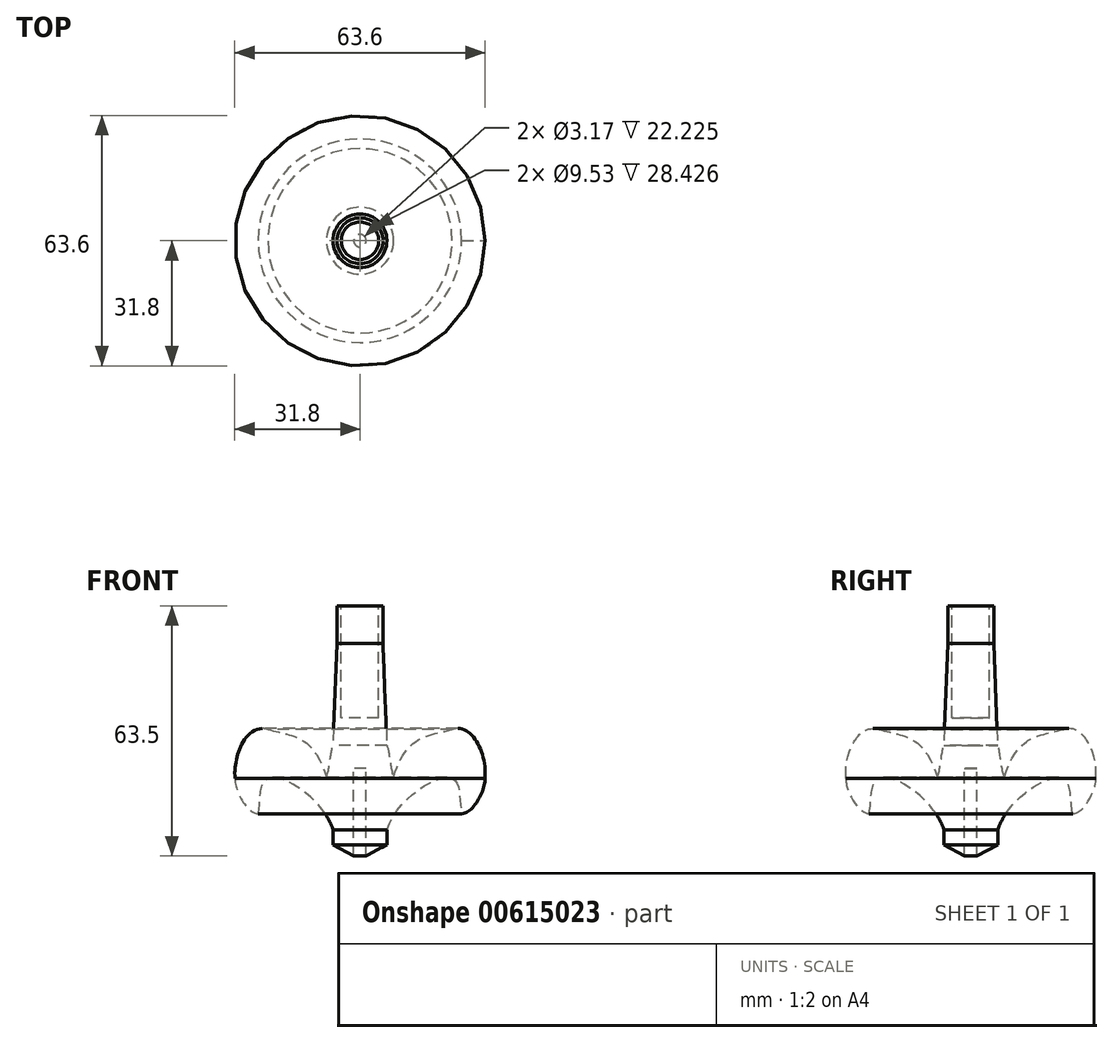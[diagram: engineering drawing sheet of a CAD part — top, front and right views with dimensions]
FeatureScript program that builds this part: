
annotation { "Feature Type Name" : "Feature", "Feature Type Description" : "" }
export const myFeature = defineFeature(function(context is Context, id is Id, definition is map)
    precondition{}
    {
        {
            var Q0;
            Q0=qCreatedBy(makeId("Front.planeOp"),FACE);
            var sketch = newSketch(context, id + "F0", { "sketchPlane" : qUnion([Q0])});
            skLineSegment(sketch, "E0", {"start": v(0, 0) * mm, "end": v(0, 22.22) * mm});
            skLineSegment(sketch, "E1", {"start": v(0, 22.23) * mm, "end": v(1.59, 22.23) * mm});
            skLineSegment(sketch, "E2", {"start": v(1.59, 22.23) * mm, "end": v(1.59, 0) * mm});
            skLineSegment(sketch, "E3", {"start": v(1.59, 0) * mm, "end": v(6.84, 2.85) * mm});
            skLineSegment(sketch, "E4", {"start": v(6.84, 2.85) * mm, "end": v(6.84, 6.58) * mm});
            skLineSegment(sketch, "E5", {"start": v(6.84, 28.12) * mm, "end": v(5.82, 53.98) * mm});
            skLineSegment(sketch, "E6", {"start": v(5.82, 53.98) * mm, "end": v(5.82, 63.5) * mm});
            skLineSegment(sketch, "E7", {"start": v(5.82, 63.5) * mm, "end": v(4.76, 63.5) * mm});
            skLineSegment(sketch, "E8", {"start": v(4.76, 63.5) * mm, "end": v(4.76, 35.07) * mm});
            skLineSegment(sketch, "E9", {"start": v(4.76, 35.07) * mm, "end": v(0, 35.07) * mm});
            skLineSegment(sketch, "E10", {"start": v(0, 35.07) * mm, "end": v(0, 0) * mm});
            skFitSpline(sketch, "E11", {"points": [v(6.84, 6.58) * mm, v(23.4, 19.68) * mm, v(25.85, 10.7) * mm], "startDerivative": vector(12.05, 39.7) * mm, "endDerivative": vector(5.56, -25) * mm});
            skPoint(sketch, "E12", {"position": v(26.1, 14.03) * mm});
            skFitSpline(sketch, "E13", {"points": [v(25.85, 10.7) * mm, v(31.75, 19.68) * mm], "startDerivative": vector(9.12, 0.6) * mm, "endDerivative": vector(-0.42, 8.68) * mm});
            skFitSpline(sketch, "E14", {"points": [v(6.84, 28.12) * mm, v(8.53, 20) * mm], "startDerivative": vector(2.06, -5.23) * mm, "endDerivative": vector(3, -8.63) * mm});
            skFitSpline(sketch, "E15", {"points": [v(8.53, 20) * mm, v(23.4, 32.13) * mm], "startDerivative": vector(9.76, 30.86) * mm, "endDerivative": vector(22.03, 5.5) * mm});
            skFitSpline(sketch, "E16", {"points": [v(31.75, 19.68) * mm, v(23.4, 32.13) * mm], "startDerivative": vector(1.59, 18.97) * mm, "endDerivative": vector(-15.55, -5.22) * mm});
            skSolve(sketch);
        }
        {
            var Q0;
            Q0 = qSketchRegion(id + "F0", true);
            var Q1;
            Q1=sQuery(id+"F0.wireOp",EDGE,"E10");
            revolve(context, id + "F1", {"entities" : qUnion([Q0]), "axis" : qUnion([Q1]), "revolveType" : RevolveType.FULL});
        }
    });
